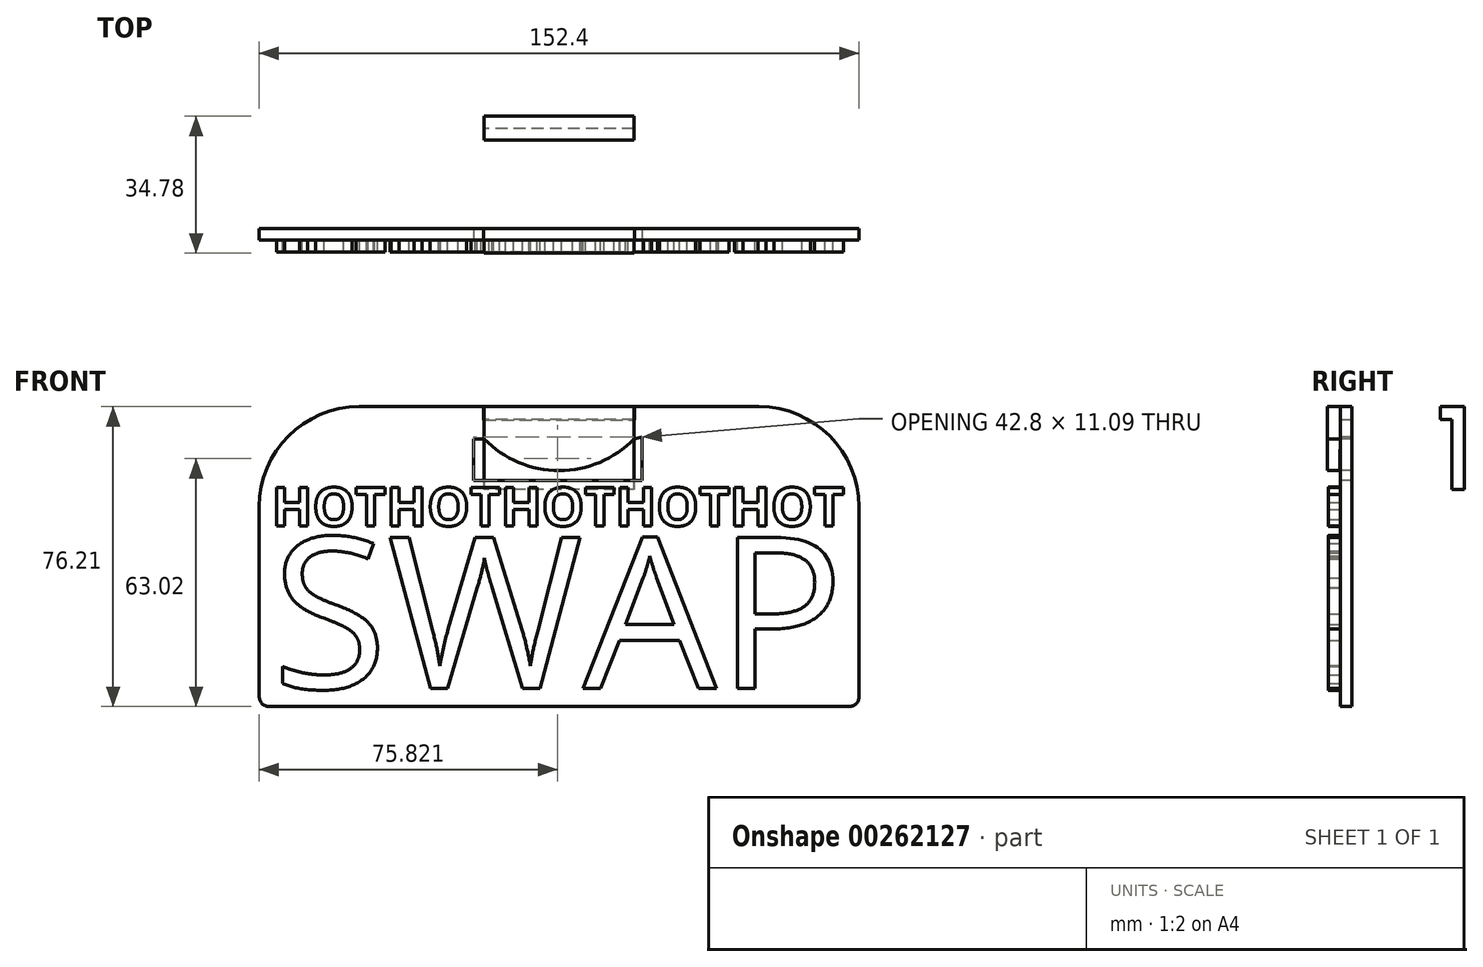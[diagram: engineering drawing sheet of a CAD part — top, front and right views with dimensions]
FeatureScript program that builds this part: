
annotation { "Feature Type Name" : "Feature", "Feature Type Description" : "" }
export const myFeature = defineFeature(function(context is Context, id is Id, definition is map)
    precondition{}
    {
        {
            var Q0;
            Q0=qCreatedBy(makeId("Front.planeOp"),FACE);
            var sketch = newSketch(context, id + "F0", { "sketchPlane" : qUnion([Q0])});
            skLineSegment(sketch, "E0.bottom", {"start": v(-2.54, 0) * mm, "end": v(-149.86, 0) * mm});
            skLineSegment(sketch, "E0.top", {"start": v(-25.4, 76.2) * mm, "end": v(-127, 76.2) * mm});
            skLineSegment(sketch, "E0.left", {"start": v(0, 2.54) * mm, "end": v(0, 50.8) * mm});
            skLineSegment(sketch, "E0.right", {"start": v(-152.4, 2.54) * mm, "end": v(-152.4, 50.8) * mm});
            skPoint(sketch, "E1.visualSharp", {"position": v(-152.4, 76.2) * mm});
            skArc(sketch, "E1.filletArc", {"start": v(-127, 76.2) * mm, "mid": v(-144.96, 68.76) * mm, "end": v(-152.4, 50.8) * mm});
            skPoint(sketch, "E2.visualSharp", {"position": v(0, 76.2) * mm});
            skArc(sketch, "E2.filletArc", {"start": v(0, 50.8) * mm, "mid": v(-7.44, 68.76) * mm, "end": v(-25.4, 76.2) * mm});
            skPoint(sketch, "E3.visualSharp", {"position": v(0, 0) * mm});
            skArc(sketch, "E3.filletArc", {"start": v(-2.54, 0) * mm, "mid": v(-0.74, 0.74) * mm, "end": v(0, 2.54) * mm});
            skPoint(sketch, "E4.visualSharp", {"position": v(-152.4, 0) * mm});
            skArc(sketch, "E4.filletArc", {"start": v(-152.4, 2.54) * mm, "mid": v(-151.66, 0.74) * mm, "end": v(-149.86, 0) * mm});
            skSolve(sketch);
        }
        {
            var Q0;
            Q0=makeQuery(id+"F0.imprint","IMPRINT",FACE,{"disambiguationData":[TD([[makeQuery(id+"F0.imprint","IMPRINT",EDGE,{"derivedFrom":sQuery(id+"F0.wireOp",EDGE,"E0.bottom")}),-1.0]])]});
            extrude(context, id + "F1", {"entities" : qUnion([Q0]), "depth" : 2.9 * mm});
        }
        {
            var Q0;
            Q0=makeQuery(id+"F1.opExtrude","CAP_FACE",FACE,{"disambiguationData":[OSD([sQuery(id+"F0.wireOp",EDGE,"E0.bottom"),sQuery(id+"F0.wireOp",EDGE,"E0.top"),sQuery(id+"F0.wireOp",EDGE,"E0.left"),sQuery(id+"F0.wireOp",EDGE,"E0.right"),sQuery(id+"F0.wireOp",EDGE,"E1.filletArc"),sQuery(id+"F0.wireOp",EDGE,"E2.filletArc"),sQuery(id+"F0.wireOp",EDGE,"E3.filletArc"),sQuery(id+"F0.wireOp",EDGE,"E4.filletArc")])],"isStart":false});
            var sketch = newSketch(context, id + "F2", { "sketchPlane" : qUnion([Q0])});
            skText(sketch, "E5", { "text": "HOTHOTHOTHOTHOT", "fontName": "OpenSans-Bold.ttf"});
            skText(sketch, "E6", { "text": "SWAP", "fontName": "OpenSans-Regular.ttf"});
            const initialGuessF2  = {"E5": [-0.14922, 0.04592, 1, 0, 0.00979], "E6": [-0.14923, 0.00467, 1, 0, 0.03862]};
            skSetInitialGuess(sketch, initialGuessF2);
            skSolve(sketch);
        }
        {
            var Q0;
            Q0 = qSketchRegion(id + "F2", true);
            extrude(context, id + "F3", {"entities" : qUnion([Q0]), "operationType" : NewBodyOperationType.ADD, "depth" : 3 * mm});
        }
        {
            var Q0;
            Q0=qCreatedBy(makeId("Right.planeOp"),FACE);
            cPlane(context, id + "F4", {"entities" : qUnion([Q0]), "cplaneType" : CPlaneType.OFFSET, "offset" : 76.2 * mm, "oppositeDirection" : true, "width" : 152.4 * mm, "height" : 152.4 * mm});
        }
        {
            var Q0;
            Q0=qCreatedBy(id+"F4.planeOp",FACE);
            var sketch = newSketch(context, id + "F5", { "sketchPlane" : qUnion([Q0])});
            skLineSegment(sketch, "E7", {"start": v(-6.2, 76.2) * mm, "end": v(28.57, 76.2) * mm});
            skLineSegment(sketch, "E8", {"start": v(28.57, 76.2) * mm, "end": v(28.57, 55.2) * mm});
            skLineSegment(sketch, "E9", {"start": v(28.57, 55.2) * mm, "end": v(25.4, 55.2) * mm});
            skLineSegment(sketch, "E10", {"start": v(25.4, 55.2) * mm, "end": v(25.4, 72.98) * mm});
            skLineSegment(sketch, "E11", {"start": v(25.4, 72.98) * mm, "end": v(-2.9, 72.98) * mm});
            skLineSegment(sketch, "E12", {"start": v(-6.2, 76.2) * mm, "end": v(-6.2, 59.83) * mm});
            skLineSegment(sketch, "E13", {"start": v(-6.2, 59.83) * mm, "end": v(-2.97, 59.83) * mm});
            skLineSegment(sketch, "E14", {"start": v(-2.97, 59.83) * mm, "end": v(-2.9, 72.98) * mm});
            skSolve(sketch);
        }
        {
            var Q0;
            Q0 = qSketchRegion(id + "F5", true);
            extrude(context, id + "F6", {"entities" : qUnion([Q0]), "endBound" : BoundingType.SYMMETRIC, "depth" : 38.1 * mm});
        }
        {
            var Q0;
            {var subQ0=sQuery(id+"F0.wireOp",EDGE,"E0.bottom");var subQ1=sQuery(id+"F0.wireOp",EDGE,"E0.right");var subQ2=sQuery(id+"F0.wireOp",EDGE,"E0.left");var subQ3=sQuery(id+"F0.wireOp",EDGE,"E0.top");var subQ4=sQuery(id+"F0.wireOp",EDGE,"E4.filletArc");var subQ5=sQuery(id+"F0.wireOp",EDGE,"E3.filletArc");var subQ6=sQuery(id+"F0.wireOp",EDGE,"E2.filletArc");var subQ7=sQuery(id+"F0.wireOp",EDGE,"E1.filletArc");Q0=makeQuery(id+"F3.boolean.opBoolean","SPLIT",FACE,{"disambiguationData":[TD([makeQuery(id+"F1.opExtrude","SWEPT_FACE",FACE,{"disambiguationData":[OSD([subQ0])]})])],"derivedFrom":makeQuery(id+"F1.opExtrude","CAP_FACE",FACE,{"disambiguationData":[OSD([subQ0,subQ3,subQ2,subQ1,subQ7,subQ6,subQ5,subQ4])],"isStart":false})});}
            var sketch = newSketch(context, id + "F7", { "sketchPlane" : qUnion([Q0])});
            skLineSegment(sketch, "E15.bottom", {"start": v(-95.38, 76.2) * mm, "end": v(-57.06, 76.2) * mm});
            skLineSegment(sketch, "E15.top", {"start": v(-95.38, 72.8) * mm, "end": v(-57.06, 72.8) * mm});
            skLineSegment(sketch, "E15.left", {"start": v(-95.38, 76.2) * mm, "end": v(-95.38, 72.8) * mm});
            skLineSegment(sketch, "E15.right", {"start": v(-57.06, 76.2) * mm, "end": v(-57.06, 72.8) * mm});
            skSolve(sketch);
        }
        {
            var Q0;
            Q0 = qSketchRegion(id + "F7", true);
            extrude(context, id + "F8", {"entities" : qUnion([Q0]), "operationType" : NewBodyOperationType.REMOVE, "oppositeDirection" : true, "depth" : 25.4 * mm});
        }
        {
            var Q0;
            Q0=makeQuery(id+"F6.opExtrude","SWEPT_FACE",FACE,{"disambiguationData":[OSD([sQuery(id+"F5.wireOp",EDGE,"E12")])]});
            var sketch = newSketch(context, id + "F9", { "sketchPlane" : qUnion([Q0])});
            skArc(sketch, "E16", {"start": v(-95.25, 68.02) * mm, "mid": v(-76.2, 59.97) * mm, "end": v(-57.15, 68.02) * mm});
            skLineSegment(sketch, "E17", {"start": v(-95.25, 68.02) * mm, "end": v(-97.98, 68.02) * mm});
            skLineSegment(sketch, "E18", {"start": v(-97.98, 68.02) * mm, "end": v(-97.98, 57.48) * mm});
            skLineSegment(sketch, "E19", {"start": v(-97.98, 57.48) * mm, "end": v(-55.18, 57.48) * mm});
            skLineSegment(sketch, "E20", {"start": v(-55.18, 57.48) * mm, "end": v(-55.18, 68.56) * mm});
            skLineSegment(sketch, "E21", {"start": v(-55.18, 68.56) * mm, "end": v(-57.15, 68.02) * mm});
            skSolve(sketch);
        }
        {
            var Q0;
            Q0 = qSketchRegion(id + "F9", true);
            extrude(context, id + "F10", {"entities" : qUnion([Q0]), "operationType" : NewBodyOperationType.REMOVE, "oppositeDirection" : true, "depth" : 25.4 * mm});
        }
    });
